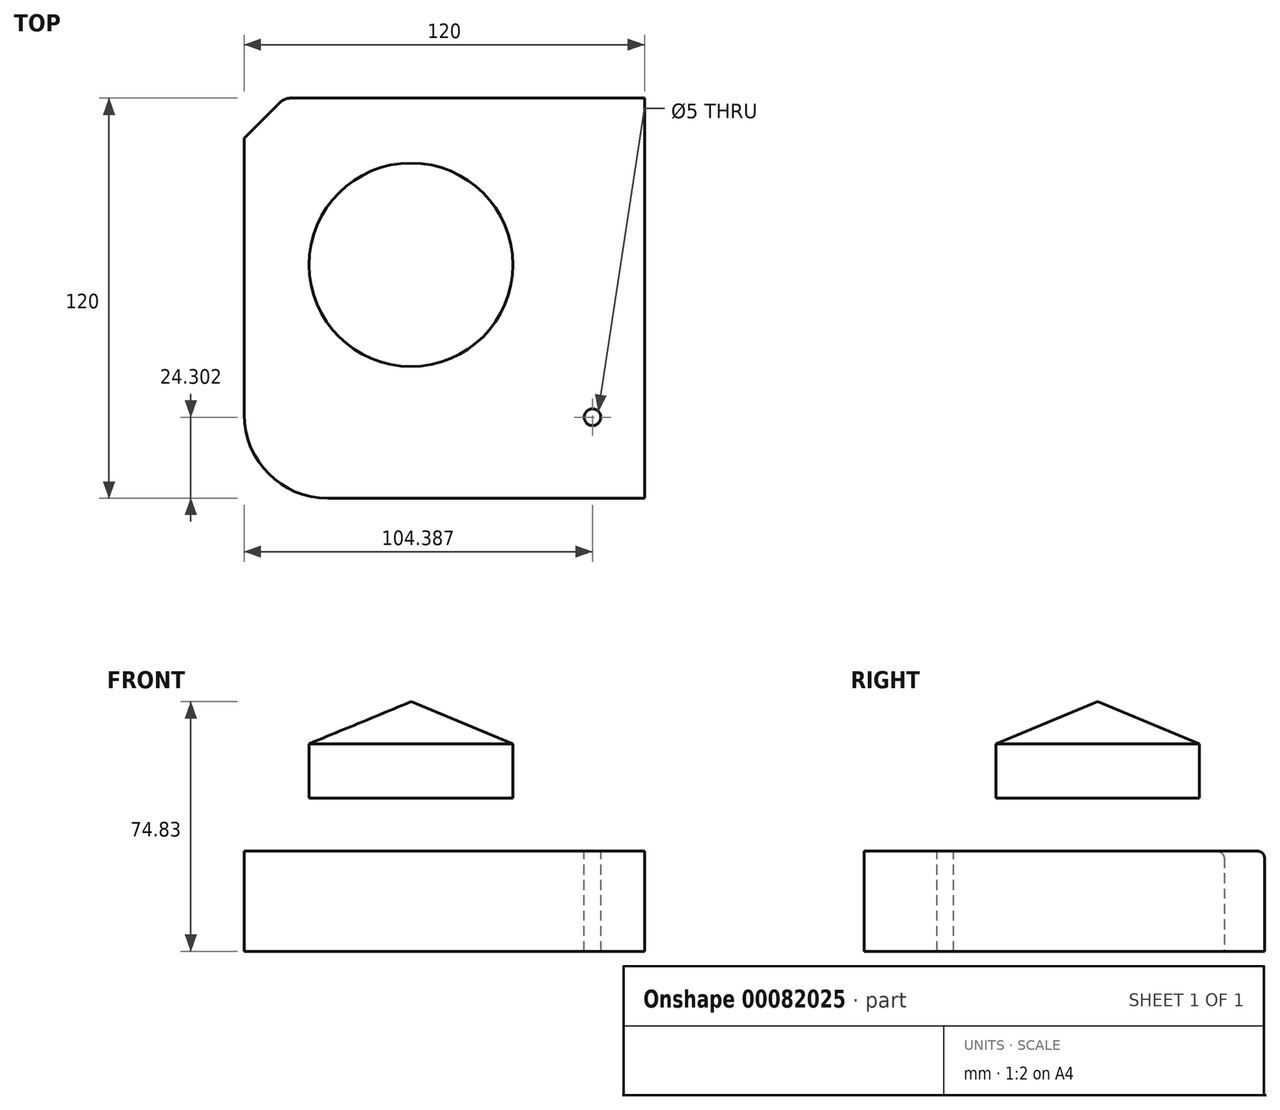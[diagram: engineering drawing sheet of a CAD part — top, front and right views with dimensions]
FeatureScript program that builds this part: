
annotation { "Feature Type Name" : "Feature", "Feature Type Description" : "" }
export const myFeature = defineFeature(function(context is Context, id is Id, definition is map)
    precondition{}
    {
        {
            var Q0;
            Q0=qCreatedBy(makeId("Top.planeOp"),FACE);
            var sketch = newSketch(context, id + "F0", { "sketchPlane" : qUnion([Q0])});
            skLineSegment(sketch, "E0.bottom", {"start": v(-35.93, 50) * mm, "end": v(70, 50) * mm});
            skLineSegment(sketch, "E0.top", {"start": v(-25, -70) * mm, "end": v(70, -70) * mm});
            skLineSegment(sketch, "E0.left", {"start": v(-50, 38) * mm, "end": v(-50, -45) * mm});
            skLineSegment(sketch, "E0.right", {"start": v(70, 50) * mm, "end": v(70, -70) * mm});
            skLineSegment(sketch, "E1", {"start": v(-50, 38) * mm, "end": v(-39.46, 48.54) * mm});
            skPoint(sketch, "E2.visualSharp", {"position": v(-38, 50) * mm});
            skArc(sketch, "E2.filletArc", {"start": v(-35.93, 50) * mm, "mid": v(-37.84, 49.62) * mm, "end": v(-39.46, 48.54) * mm});
            skPoint(sketch, "E3.visualSharp", {"position": v(-50, -70) * mm});
            skArc(sketch, "E3.filletArc", {"start": v(-50, -45) * mm, "mid": v(-42.68, -62.68) * mm, "end": v(-25, -70) * mm});
            skSolve(sketch);
        }
        {
            var Q0;
            Q0 = qSketchRegion(id + "F0", true);
            extrude(context, id + "F1", {"entities" : qUnion([Q0]), "depth" : 25 * mm});
        }
        {
            var Q0;
            Q0 = qSketchRegion(id + "F0", true);
            extrude(context, id + "F2", {"entities" : qUnion([Q0]), "operationType" : NewBodyOperationType.ADD, "oppositeDirection" : true, "depth" : 5 * mm});
        }
        {
            var Q0;
            Q0=qCreatedBy(makeId("Right.planeOp"),FACE);
            var sketch = newSketch(context, id + "F3", { "sketchPlane" : qUnion([Q0])});
            skLineSegment(sketch, "E4", {"start": v(0, 40.9) * mm, "end": v(-30.53, 40.9) * mm});
            skLineSegment(sketch, "E5", {"start": v(-30.53, 40.9) * mm, "end": v(-30.53, 57.22) * mm});
            skLineSegment(sketch, "E6", {"start": v(-30.53, 57.22) * mm, "end": v(0, 69.83) * mm});
            skLineSegment(sketch, "E7", {"start": v(0, 69.83) * mm, "end": v(0, 40.9) * mm});
            skSolve(sketch);
        }
        {
            var Q0;
            Q0 = qSketchRegion(id + "F3", true);
            var Q1;
            Q1=sQuery(id+"F3.wireOp",EDGE,"E7");
            revolve(context, id + "F4", {"entities" : qUnion([Q0]), "axis" : qUnion([Q1]), "revolveType" : RevolveType.FULL});
        }
        {
            var Q0;
            Q0=makeQuery(id+"F1.opExtrude","CAP_EDGE",EDGE,{"disambiguationData":[OSD([sQuery(id+"F0.wireOp",EDGE,"E0.bottom")])],"isStart":false});
            fillet(context, id + "F5", {"entities" : qUnion([Q0]), "radius" : 2 * mm, "tangentPropagation" : true, "allowEdgeOverflow" : false});
        }
        {
            var Q0;
            Q0=makeQuery(id+"F1.opExtrude","CAP_FACE",FACE,{"disambiguationData":[OSD([sQuery(id+"F0.wireOp",EDGE,"E0.bottom"),sQuery(id+"F0.wireOp",EDGE,"E0.top"),sQuery(id+"F0.wireOp",EDGE,"E0.left"),sQuery(id+"F0.wireOp",EDGE,"E0.right"),sQuery(id+"F0.wireOp",EDGE,"E1"),sQuery(id+"F0.wireOp",EDGE,"E2.filletArc"),sQuery(id+"F0.wireOp",EDGE,"E3.filletArc")])],"isStart":false});
            var sketch = newSketch(context, id + "F6", { "sketchPlane" : qUnion([Q0])});
            skCircle(sketch, "E8", {"center": v(54.39, -45.7) * mm, "radius": 4.64 * mm});
            skSolve(sketch);
        }
        {
            var Q0;
            Q0=sQuery(id+"F6.wireOp",VERTEX,"E8.center");
            var Q1;
            Q1=makeQuery(id+"F1.opExtrude","SWEPT_BODY",BODY,{"disambiguationData":[OSD([sQuery(id+"F0.wireOp",EDGE,"E0.bottom"),sQuery(id+"F0.wireOp",EDGE,"E0.top"),sQuery(id+"F0.wireOp",EDGE,"E0.left"),sQuery(id+"F0.wireOp",EDGE,"E0.right"),sQuery(id+"F0.wireOp",EDGE,"E1"),sQuery(id+"F0.wireOp",EDGE,"E2.filletArc"),sQuery(id+"F0.wireOp",EDGE,"E3.filletArc")])]});
            hole(context, id + "F7", {"style" : HoleStyle.SIMPLE, "endStyle" : HoleEndStyle.THROUGH, "holeDiameter" : 5 * mm, "locations" : qUnion([Q0]), "scope" : qUnion([Q1]), "isTappedThrough" : true});
        }
        {
            var Q0;
            {var subQ0=sQuery(id+"F0.wireOp",EDGE,"E0.right");var subQ1=sQuery(id+"F0.wireOp",EDGE,"E0.top");Q0=makeQuery(id+"F2.boolean.opBoolean","MERGE",EDGE,{"derivedFrom":[makeQuery(id+"F1.opExtrude","SWEPT_EDGE",EDGE,{"disambiguationData":[OSD([subQ1,subQ0])]}),makeQuery(id+"F2.opExtrude","SWEPT_EDGE",EDGE,{"disambiguationData":[OSD([subQ1,subQ0])]})]});}
            var Q1;
            Q1=makeQuery(id+"F2.opExtrude","CAP_VERTEX",VERTEX,{"disambiguationData":[OSD([sQuery(id+"F0.wireOp",EDGE,"E0.top"),sQuery(id+"F0.wireOp",EDGE,"E3.filletArc")])],"isStart":false});
            cPlane(context, id + "F8", {"entities" : qUnion([Q0, Q1]), "cplaneType" : CPlaneType.LINE_ANGLE, "offset" : 50 * mm, "angle" : 45 * degree, "width" : 150 * mm, "height" : 150 * mm});
        }
    });
